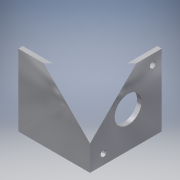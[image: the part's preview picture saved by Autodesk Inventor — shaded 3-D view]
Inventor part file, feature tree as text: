
AUTODESK INVENTOR PART (.ipt)
format: ipt  version: 2016 (Build 200138000, 138)  size: 121,856 bytes
history: native  units: in
note: dims shown in document units (in); Inventor stores cm internally (conversion verified against a paired STEP export)
features: extrude x2, sketch x2
ambient origin geometry x8: Origin, YZ Plane, XZ Plane, XY Plane, X Axis, Y Axis, Z Axis, Center Point
bodies: Solid1 (feature_tree)
feature tree (4):
  extrude  "Extrusion1"  Depth=2.0in
  extrude  "Extrusion2"  Depth=1.875in
  sketch  "Sketch1"  dims[d0=2.0in d1=2.0in]
  sketch  "Sketch3"  dims[d2=0.125in d3=1.875in d4=1.875in d5=2.0in d6=0.0in d12=2.0in d13=1.0in d14=0.9375in d15=0.16in d16=0.16in d17=0.689in d18=0.689in d19=0.75in d20=0.125in d21=0.0in]
